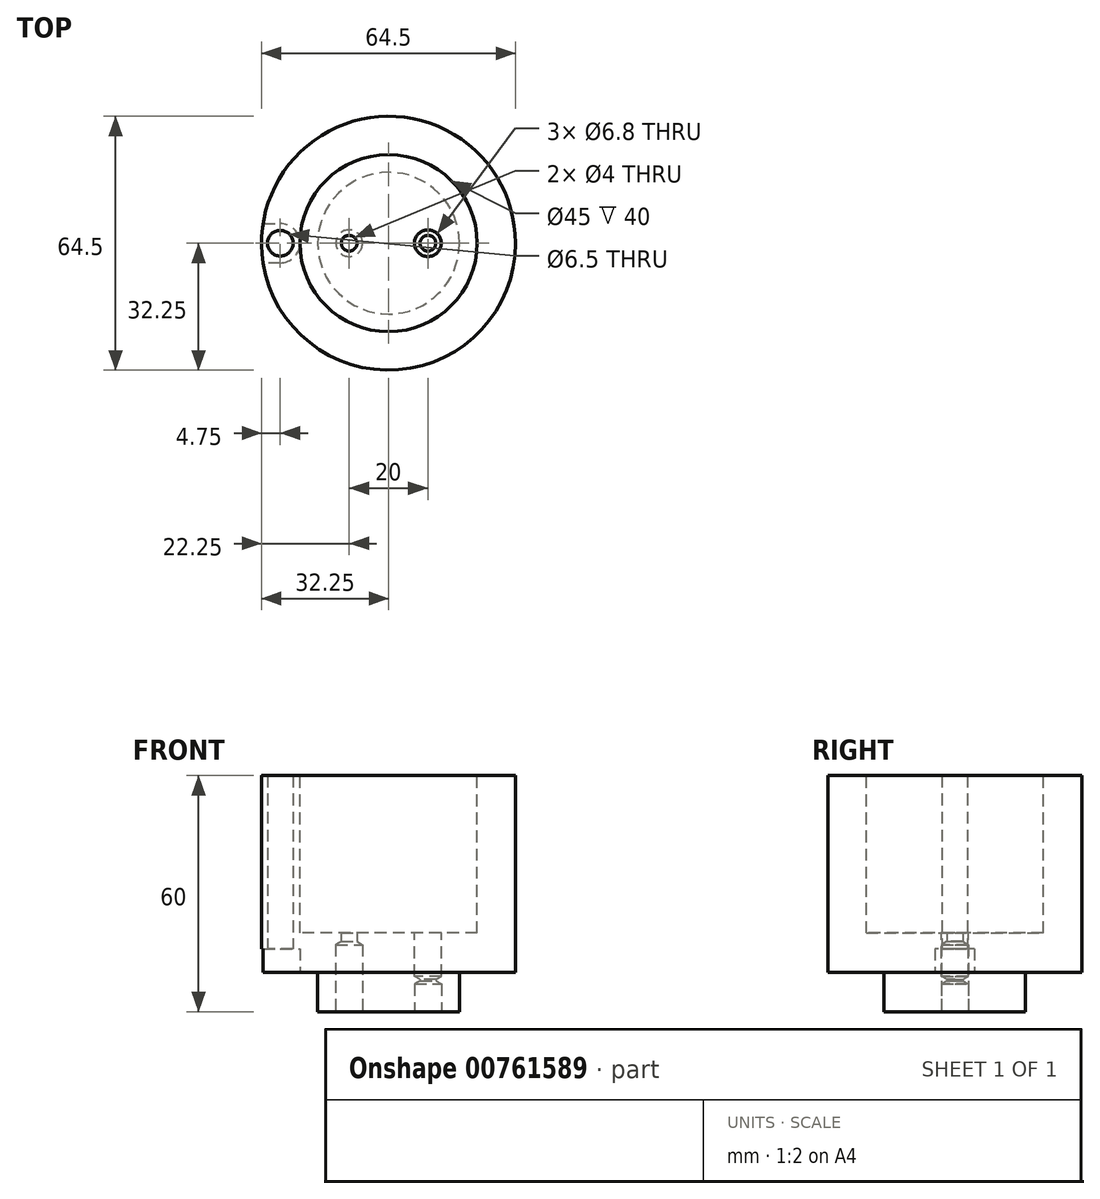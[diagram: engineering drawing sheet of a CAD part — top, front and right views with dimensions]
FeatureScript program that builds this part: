
annotation { "Feature Type Name" : "Feature", "Feature Type Description" : "" }
export const myFeature = defineFeature(function(context is Context, id is Id, definition is map)
    precondition{}
    {
        {
            var Q0;
            Q0=qCreatedBy(makeId("Top.planeOp"),FACE);
            var sketch = newSketch(context, id + "F0", { "sketchPlane" : qUnion([Q0])});
            skCircle(sketch, "E0", {"center": v(0, 0) * mm, "radius": 32.25 * mm});
            skSolve(sketch);
        }
        {
            var Q0;
            Q0 = qSketchRegion(id + "F0", true);
            extrude(context, id + "F1", {"entities" : qUnion([Q0]), "depth" : 50 * mm, "offsetDistance" : 25 * mm});
        }
        {
            var Q0;
            Q0=makeQuery(id+"F1.opExtrude","CAP_FACE",FACE,{"disambiguationData":[OSD([sQuery(id+"F0.wireOp",EDGE,"E0")])],"isStart":false});
            var sketch = newSketch(context, id + "F2", { "sketchPlane" : qUnion([Q0])});
            skCircle(sketch, "E1", {"center": v(0, 0) * mm, "radius": 22.5 * mm});
            skSolve(sketch);
        }
        {
            var Q0;
            Q0 = qSketchRegion(id + "F2", true);
            extrude(context, id + "F3", {"entities" : qUnion([Q0]), "operationType" : NewBodyOperationType.REMOVE, "oppositeDirection" : true, "depth" : 40 * mm, "offsetDistance" : 25 * mm});
        }
        {
            var Q0;
            Q0=qCreatedBy(makeId("Top.planeOp"),FACE);
            var sketch = newSketch(context, id + "F4", { "sketchPlane" : qUnion([Q0])});
            skCircle(sketch, "E2", {"center": v(0, 0) * mm, "radius": 18 * mm});
            skSolve(sketch);
        }
        {
            var Q0;
            Q0 = qSketchRegion(id + "F4", true);
            extrude(context, id + "F5", {"entities" : qUnion([Q0]), "operationType" : NewBodyOperationType.ADD, "oppositeDirection" : true, "depth" : 10 * mm, "offsetDistance" : 25 * mm});
        }
        {
            var Q0;
            Q0=qCreatedBy(makeId("Top.planeOp"),FACE);
            var sketch = newSketch(context, id + "F6", { "sketchPlane" : qUnion([Q0])});
            skArc(sketch, "E3", {"start": v(-27.5, -5) * mm, "mid": v(-22.5, 0) * mm, "end": v(-27.5, 5) * mm});
            skLineSegment(sketch, "E4", {"start": v(-27.5, -5) * mm, "end": v(-35, -5) * mm});
            skLineSegment(sketch, "E5", {"start": v(-35, -5) * mm, "end": v(-35, 5) * mm});
            skLineSegment(sketch, "E6", {"start": v(-35, 5) * mm, "end": v(-27.5, 5) * mm});
            skSolve(sketch);
        }
        {
            var Q0;
            Q0 = qSketchRegion(id + "F6", true);
            extrude(context, id + "F7", {"entities" : qUnion([Q0]), "operationType" : NewBodyOperationType.REMOVE, "depth" : 6 * mm, "offsetDistance" : 25 * mm});
        }
        {
            var Q0;
            Q0=sQuery(id+"F6.wireOp",VERTEX,"E3.center");
            var Q1;
            Q1=makeQuery(id+"F1.opExtrude","SWEPT_BODY",BODY,{"disambiguationData":[OSD([sQuery(id+"F0.wireOp",EDGE,"E0")])]});
            hole(context, id + "F8", {"style" : HoleStyle.SIMPLE, "endStyle" : HoleEndStyle.THROUGH, "oppositeDirection" : true, "holeDiameter" : 6.5 * mm, "majorDiameter" : 8 * mm, "isTappedThrough" : true, "tappedDepth" : 18 * mm, "tapClearance" : 4, "startFromSketch" : true, "locations" : qUnion([Q0]), "scope" : qUnion([Q1])});
        }
        {
            var Q0;
            Q0=makeQuery(id+"F5.opExtrude","CAP_FACE",FACE,{"disambiguationData":[OSD([sQuery(id+"F4.wireOp",EDGE,"E2")])],"isStart":false});
            var sketch = newSketch(context, id + "F9", { "sketchPlane" : qUnion([Q0])});
            skPoint(sketch, "E7", {"position": v(-10, 0) * mm});
            skPoint(sketch, "E8", {"position": v(10, 0) * mm});
            skSolve(sketch);
        }
        {
            var Q0;
            Q0=sQuery(id+"F9.wireOp",VERTEX,"E7");
            var Q1;
            Q1=sQuery(id+"F9.wireOp",VERTEX,"E8");
            var Q2;
            Q2=makeQuery(id+"F1.opExtrude","SWEPT_BODY",BODY,{"disambiguationData":[OSD([sQuery(id+"F0.wireOp",EDGE,"E0")])]});
            hole(context, id + "F10", {"style" : HoleStyle.SIMPLE, "endStyle" : HoleEndStyle.THROUGH, "holeDiameter" : 4 * mm, "majorDiameter" : 5 * mm, "isTappedThrough" : true, "tappedDepth" : 18 * mm, "tapClearance" : 4, "startFromSketch" : true, "locations" : qUnion([Q0, Q1]), "scope" : qUnion([Q2])});
        }
        {
            var Q0;
            Q0=sQuery(id+"F9.wireOp",VERTEX,"E7");
            var Q1;
            Q1=makeQuery(id+"F1.opExtrude","SWEPT_BODY",BODY,{"disambiguationData":[OSD([sQuery(id+"F0.wireOp",EDGE,"E0")])]});
            hole(context, id + "F11", {"style" : HoleStyle.SIMPLE, "endStyle" : HoleEndStyle.BLIND, "standardTappedOrClearance" : lookupTablePath({ "standard" : "ISO", "engagement" : "75%", "pitch" : "1.25 mm", "size" : "M8", "type" : "Tapped" }), "standardBlindInLast" : lookupTablePath({ "standard" : "ISO", "engagement" : "75%", "pitch" : "1.25 mm", "size" : "M8", "type" : "Tapped" }), "holeDiameter" : 6.8 * mm, "majorDiameter" : 8 * mm, "showTappedDepth" : true, "holeDepth" : 17 * mm, "tappedDepth" : 17 * mm, "tapClearance" : 0, "startFromSketch" : true, "locations" : qUnion([Q0]), "scope" : qUnion([Q1])});
        }
        {
            var Q0;
            Q0=sQuery(id+"F9.wireOp",VERTEX,"E8");
            var Q1;
            Q1=makeQuery(id+"F1.opExtrude","SWEPT_BODY",BODY,{"disambiguationData":[OSD([sQuery(id+"F0.wireOp",EDGE,"E0")])]});
            hole(context, id + "F12", {"style" : HoleStyle.SIMPLE, "endStyle" : HoleEndStyle.BLIND, "standardTappedOrClearance" : lookupTablePath({ "standard" : "ISO", "engagement" : "75%", "pitch" : "1.25 mm", "size" : "M8", "type" : "Tapped" }), "standardBlindInLast" : lookupTablePath({ "standard" : "ISO", "engagement" : "75%", "pitch" : "1.25 mm", "size" : "M8", "type" : "Tapped" }), "holeDiameter" : 6.8 * mm, "majorDiameter" : 8 * mm, "showTappedDepth" : true, "holeDepth" : 7 * mm, "tappedDepth" : 7 * mm, "tapClearance" : 0, "startFromSketch" : true, "locations" : qUnion([Q0]), "scope" : qUnion([Q1])});
        }
        {
            var Q0;
            Q0=makeQuery(id+"F3.boolean.opBoolean","COPY",FACE,{"derivedFrom":makeQuery(id+"F3.opExtrude","CAP_FACE",FACE,{"disambiguationData":[OSD([sQuery(id+"F2.wireOp",EDGE,"E1")])],"isStart":false})});
            var sketch = newSketch(context, id + "F13", { "sketchPlane" : qUnion([Q0])});
            skPoint(sketch, "E9.0", {"position": v(10, 0) * mm});
            skSolve(sketch);
        }
        {
            var Q0;
            Q0=sQuery(id+"F13.wireOp",VERTEX,"E9.0");
            var Q1;
            Q1=makeQuery(id+"F1.opExtrude","SWEPT_BODY",BODY,{"disambiguationData":[OSD([sQuery(id+"F0.wireOp",EDGE,"E0")])]});
            hole(context, id + "F14", {"style" : HoleStyle.SIMPLE, "endStyle" : HoleEndStyle.BLIND, "standardTappedOrClearance" : lookupTablePath({ "standard" : "ISO", "engagement" : "75%", "pitch" : "1.25 mm", "size" : "M8", "type" : "Tapped" }), "standardBlindInLast" : lookupTablePath({ "standard" : "ISO", "engagement" : "75%", "pitch" : "1.25 mm", "size" : "M8", "type" : "Tapped" }), "holeDiameter" : 6.8 * mm, "majorDiameter" : 8 * mm, "showTappedDepth" : true, "holeDepth" : 11 * mm, "tappedDepth" : 11 * mm, "tapClearance" : 0, "startFromSketch" : true, "locations" : qUnion([Q0]), "scope" : qUnion([Q1])});
        }
    });
